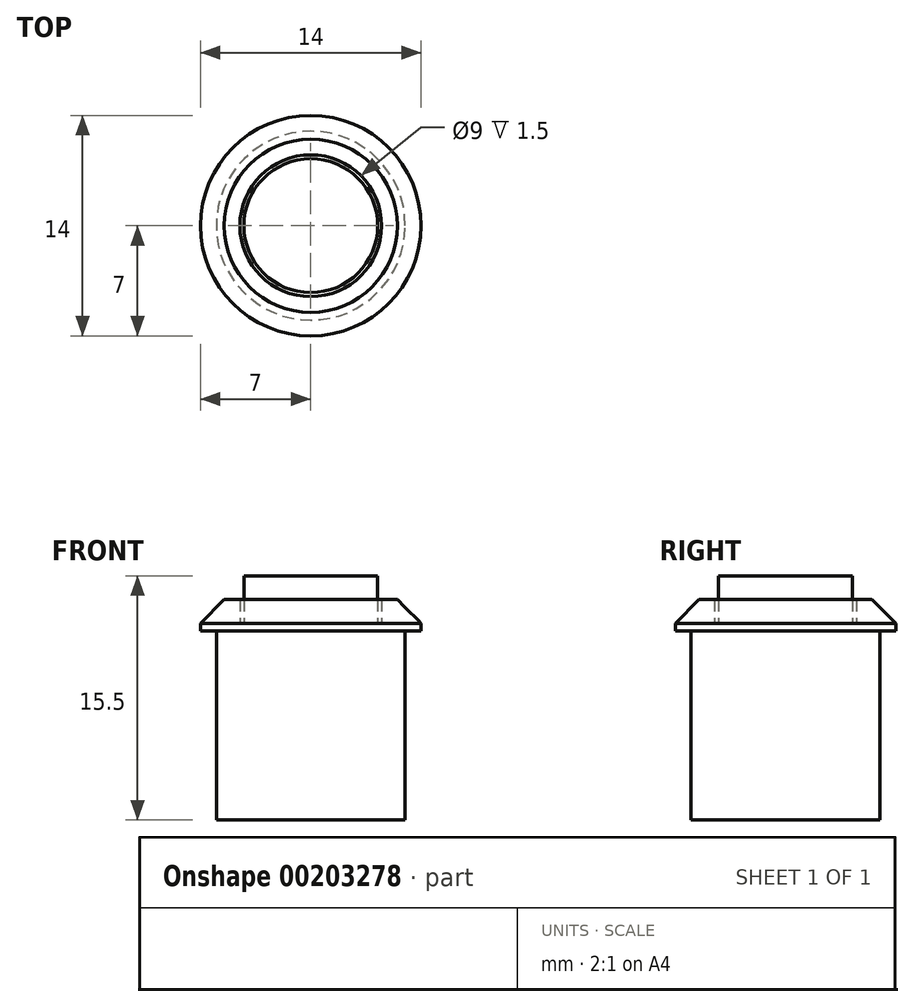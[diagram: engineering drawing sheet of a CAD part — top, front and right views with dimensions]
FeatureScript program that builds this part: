
annotation { "Feature Type Name" : "Feature", "Feature Type Description" : "" }
export const myFeature = defineFeature(function(context is Context, id is Id, definition is map)
    precondition{}
    {
        {
            var Q0;
            Q0=qCreatedBy(makeId("Top.planeOp"),FACE);
            var sketch = newSketch(context, id + "F0", { "sketchPlane" : qUnion([Q0])});
            skCircle(sketch, "E0", {"center": v(0, 0) * mm, "radius": 7 * mm});
            skCircle(sketch, "E1", {"center": v(0, 0) * mm, "radius": 4.5 * mm});
            skCircle(sketch, "E2", {"center": v(0, 0) * mm, "radius": 6 * mm});
            skSolve(sketch);
        }
        {
            var Q0;
            Q0=makeQuery(id+"F0.imprint","IMPRINT",FACE,{"disambiguationData":[TD([[makeQuery(id+"F0.imprint","IMPRINT",EDGE,{"derivedFrom":sQuery(id+"F0.wireOp",EDGE,"E0")}),1.0]])]});
            var Q1;
            Q1=makeQuery(id+"F0.imprint","IMPRINT",FACE,{"disambiguationData":[TD([[makeQuery(id+"F0.imprint","IMPRINT",EDGE,{"derivedFrom":sQuery(id+"F0.wireOp",EDGE,"E1")}),-1.0]])]});
            extrude(context, id + "F1", {"entities" : qUnion([Q0, Q1]), "depth" : 2 * mm});
        }
        {
            var Q0;
            Q0=makeQuery(id+"F1.opExtrude","CAP_EDGE",EDGE,{"disambiguationData":[OSD([sQuery(id+"F0.wireOp",EDGE,"E0")])],"isStart":false});
            chamfer(context, id + "F2", {"entities" : qUnion([Q0]), "width" : 1.5 * mm, "tangentPropagation" : true});
        }
        {
            var Q0;
            Q0=makeQuery(id+"F0.imprint","IMPRINT",FACE,{"disambiguationData":[TD([[makeQuery(id+"F0.imprint","IMPRINT",EDGE,{"derivedFrom":sQuery(id+"F0.wireOp",EDGE,"E1")}),1.0]])]});
            extrude(context, id + "F3", {"entities" : qUnion([Q0]), "operationType" : NewBodyOperationType.ADD, "depth" : .5 * mm});
        }
        {
            var Q0;
            Q0=makeQuery(id+"F3.opExtrude","CAP_FACE",FACE,{"disambiguationData":[OSD([sQuery(id+"F0.wireOp",EDGE,"E1")])],"isStart":false});
            var sketch = newSketch(context, id + "F4", { "sketchPlane" : qUnion([Q0])});
            skCircle(sketch, "E3", {"center": v(0, 0) * mm, "radius": 4.25 * mm});
            skSolve(sketch);
        }
        {
            var Q0;
            Q0=makeQuery(id+"F4.imprint","IMPRINT",FACE,{"disambiguationData":[TD([[makeQuery(id+"F4.imprint","IMPRINT",EDGE,{"derivedFrom":sQuery(id+"F4.wireOp",EDGE,"E3")}),1.0]])]});
            extrude(context, id + "F5", {"entities" : qUnion([Q0]), "operationType" : NewBodyOperationType.ADD, "depth" : 3 * mm});
        }
        {
            var Q0;
            Q0=makeQuery(id+"F0.imprint","IMPRINT",FACE,{"disambiguationData":[TD([[makeQuery(id+"F0.imprint","IMPRINT",EDGE,{"derivedFrom":sQuery(id+"F0.wireOp",EDGE,"E1")}),-1.0]])]});
            var Q1;
            Q1=makeQuery(id+"F0.imprint","IMPRINT",FACE,{"disambiguationData":[TD([[makeQuery(id+"F0.imprint","IMPRINT",EDGE,{"derivedFrom":sQuery(id+"F0.wireOp",EDGE,"E1")}),1.0]])]});
            extrude(context, id + "F6", {"entities" : qUnion([Q0, Q1]), "operationType" : NewBodyOperationType.ADD, "oppositeDirection" : true, "depth" : 12 * mm});
        }
    });
